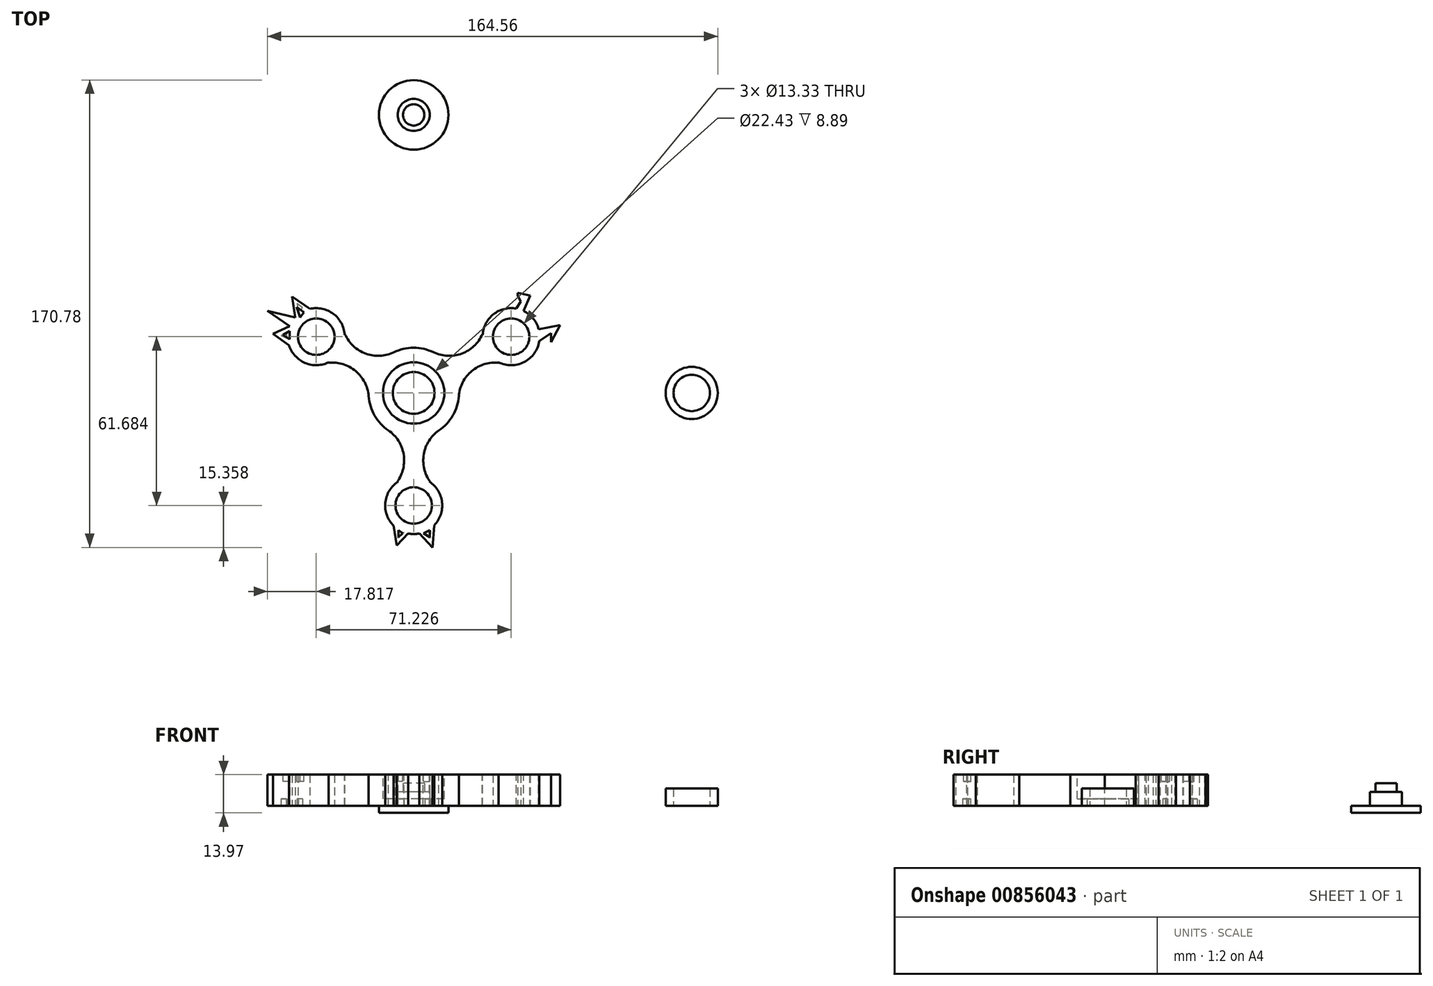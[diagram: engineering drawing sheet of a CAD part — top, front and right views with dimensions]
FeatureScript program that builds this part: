
annotation { "Feature Type Name" : "Feature", "Feature Type Description" : "" }
export const myFeature = defineFeature(function(context is Context, id is Id, definition is map)
    precondition{}
    {
        {
            var Q0;
            Q0=qCreatedBy(makeId("Top.planeOp"),FACE);
            var sketch = newSketch(context, id + "F0", { "sketchPlane" : qUnion([Q0])});
            skCircle(sketch, "E0", {"center": v(0, 101.6) * mm, "radius": 5.85 * mm});
            skSolve(sketch);
        }
        {
            var Q0;
            Q0=qSketchRegion(id+"F0",true);
            extrude(context, id + "F1", {"entities" : qUnion([Q0]), "depth" : 5.08 * mm, "offsetDistance" : 25.4 * mm});
        }
        {
            var Q0;
            Q0=makeQuery(id+"F1.opExtrude","CAP_FACE",FACE,{"disambiguationData":[OSD([sQuery(id+"F0.wireOp",EDGE,"E0")])],"isStart":false});
            var sketch = newSketch(context, id + "F2", { "sketchPlane" : qUnion([Q0])});
            skCircle(sketch, "E1", {"center": v(0, 101.6) * mm, "radius": 3.9 * mm});
            skSolve(sketch);
        }
        {
            var Q0;
            Q0=qSketchRegion(id+"F2",true);
            extrude(context, id + "F3", {"entities" : qUnion([Q0]), "operationType" : NewBodyOperationType.ADD, "depth" : 3.17 * mm, "offsetDistance" : 25.4 * mm});
        }
        {
            var Q0;
            Q0=makeQuery(id+"F1.opExtrude","CAP_FACE",FACE,{"disambiguationData":[OSD([sQuery(id+"F0.wireOp",EDGE,"E0")])],"isStart":true});
            var sketch = newSketch(context, id + "F4", { "sketchPlane" : qUnion([Q0])});
            skCircle(sketch, "E2", {"center": v(0, -101.6) * mm, "radius": 12.7 * mm});
            skSolve(sketch);
        }
        {
            var Q0;
            Q0=qSketchRegion(id+"F4",true);
            extrude(context, id + "F5", {"entities" : qUnion([Q0]), "operationType" : NewBodyOperationType.ADD, "depth" : 2.54 * mm, "offsetDistance" : 25.4 * mm});
        }
        {
            var Q0;
            Q0=qCreatedBy(makeId("Top.planeOp"),FACE);
            var sketch = newSketch(context, id + "F6", { "sketchPlane" : qUnion([Q0])});
            skCircle(sketch, "E3", {"center": v(101.6, 0) * mm, "radius": 9.53 * mm});
            skCircle(sketch, "E4", {"center": v(101.6, 0) * mm, "radius": 6.67 * mm});
            skSolve(sketch);
        }
        {
            var Q0;
            Q0=qSketchRegion(id+"F6",true);
            extrude(context, id + "F7", {"entities" : qUnion([Q0]), "depth" : 6.35 * mm, "offsetDistance" : 25.4 * mm});
        }
        {
            var Q0;
            Q0=qCreatedBy(makeId("Top.planeOp"),FACE);
            var sketch = newSketch(context, id + "F8", { "sketchPlane" : qUnion([Q0])});
            skCircle(sketch, "E5", {"center": v(0, 0) * mm, "radius": 16.51 * mm});
            skCircle(sketch, "E6", {"center": v(0, 0) * mm, "radius": 7.62 * mm});
            skSolve(sketch);
        }
        {
            var Q0;
            Q0=qSketchRegion(id+"F8",true);
            extrude(context, id + "F9", {"entities" : qUnion([Q0]), "depth" : 11.43 * mm, "offsetDistance" : 25.4 * mm});
        }
        {
            var Q0;
            Q0=makeQuery(id+"F9.opExtrude","CAP_FACE",FACE,{"disambiguationData":[OSD([sQuery(id+"F8.wireOp",EDGE,"E5"),sQuery(id+"F8.wireOp",EDGE,"E6")])],"isStart":false});
            var sketch = newSketch(context, id + "F10", { "sketchPlane" : qUnion([Q0])});
            skCircle(sketch, "E7", {"center": v(0, 0) * mm, "radius": 11.21 * mm});
            skSolve(sketch);
        }
        {
            var Q0;
            Q0=qSketchRegion(id+"F10",true);
            extrude(context, id + "F11", {"entities" : qUnion([Q0]), "operationType" : NewBodyOperationType.REMOVE, "oppositeDirection" : true, "depth" : 8.9 * mm, "offsetDistance" : 25.4 * mm});
        }
        {
            var Q0;
            Q0=makeQuery(id+"F9.opExtrude","CAP_FACE",FACE,{"disambiguationData":[OSD([sQuery(id+"F8.wireOp",EDGE,"E5"),sQuery(id+"F8.wireOp",EDGE,"E6")])],"isStart":false});
            var sketch = newSketch(context, id + "F12", { "sketchPlane" : qUnion([Q0])});
            skLineSegment(sketch, "E8", {"start": v(0, -38.1) * mm, "end": v(0, 0) * mm, "construction": true});
            skLineSegment(sketch, "E9", {"start": v(9.21, -13.7) * mm, "end": v(-9.21, -13.7) * mm});
            skPoint(sketch, "E10.center", {"position": v(0, 0) * mm});
            skLineSegment(sketch, "E11.1.0", {"start": v(7.26, 14.83) * mm, "end": v(16.47, -1.13) * mm});
            skLineSegment(sketch, "E11.2.0", {"start": v(-16.47, -1.13) * mm, "end": v(-7.26, 14.83) * mm});
            skArc(sketch, "E12", {"start": v(9.21, -13.7) * mm, "mid": v(3.68, -22.38) * mm, "end": v(5.99, -32.41) * mm});
            skArc(sketch, "E13.MirrorCS", {"start": v(-9.21, -13.7) * mm, "mid": v(-3.68, -22.38) * mm, "end": v(-5.99, -32.41) * mm});
            skArc(sketch, "E14.1.0", {"start": v(7.26, 14.83) * mm, "mid": v(17.54, 14.38) * mm, "end": v(25.08, 21.4) * mm});
            skArc(sketch, "E14.1.1", {"start": v(16.47, -1.13) * mm, "mid": v(21.22, 8) * mm, "end": v(31.06, 11.02) * mm});
            skArc(sketch, "E14.2.0", {"start": v(-16.47, -1.13) * mm, "mid": v(-21.22, 8) * mm, "end": v(-31.06, 11.02) * mm});
            skArc(sketch, "E14.2.1", {"start": v(-7.26, 14.83) * mm, "mid": v(-17.54, 14.38) * mm, "end": v(-25.08, 21.4) * mm});
            skLineSegment(sketch, "E15", {"start": v(-5.99, -32.41) * mm, "end": v(5.99, -32.41) * mm});
            skLineSegment(sketch, "E16", {"start": v(25.08, 21.4) * mm, "end": v(31.06, 11.02) * mm});
            skLineSegment(sketch, "E17", {"start": v(-31.06, 11.02) * mm, "end": v(-25.08, 21.4) * mm});
            skSolve(sketch);
        }
        {
            var Q0;
            Q0=qSketchRegion(id+"F12",true);
            extrude(context, id + "F13", {"entities" : qUnion([Q0]), "operationType" : NewBodyOperationType.ADD, "oppositeDirection" : true, "depth" : 11.43 * mm, "offsetDistance" : 25.4 * mm});
        }
        {
            var Q0;
            Q0=makeQuery(id+"F13.boolean.opBoolean","MERGE",FACE,{"derivedFrom":[makeQuery(id+"F9.opExtrude","CAP_FACE",FACE,{"disambiguationData":[OSD([sQuery(id+"F8.wireOp",EDGE,"E5"),sQuery(id+"F8.wireOp",EDGE,"E6")])],"isStart":false}),makeQuery(id+"F13.opExtrude","CAP_FACE",FACE,{"disambiguationData":[OSD([sQuery(id+"F12.wireOp",EDGE,"E9"),sQuery(id+"F12.wireOp",EDGE,"E12"),sQuery(id+"F12.wireOp",EDGE,"E13.MirrorCS"),sQuery(id+"F12.wireOp",EDGE,"E15")])],"isStart":true}),makeQuery(id+"F13.opExtrude","CAP_FACE",FACE,{"disambiguationData":[OSD([sQuery(id+"F12.wireOp",EDGE,"E11.1.0"),sQuery(id+"F12.wireOp",EDGE,"E14.1.0"),sQuery(id+"F12.wireOp",EDGE,"E14.1.1"),sQuery(id+"F12.wireOp",EDGE,"E16")])],"isStart":true}),makeQuery(id+"F13.opExtrude","CAP_FACE",FACE,{"disambiguationData":[OSD([sQuery(id+"F12.wireOp",EDGE,"E11.2.0"),sQuery(id+"F12.wireOp",EDGE,"E14.2.0"),sQuery(id+"F12.wireOp",EDGE,"E14.2.1"),sQuery(id+"F12.wireOp",EDGE,"E17")])],"isStart":true})]});
            var sketch = newSketch(context, id + "F14", { "sketchPlane" : qUnion([Q0])});
            skCircle(sketch, "E18", {"center": v(0, -41.12) * mm, "radius": 10.42 * mm});
            skCircle(sketch, "E19.1.0", {"center": v(35.61, 20.56) * mm, "radius": 10.42 * mm});
            skCircle(sketch, "E19.2.0", {"center": v(-35.61, 20.56) * mm, "radius": 10.42 * mm});
            skPoint(sketch, "E19.center", {"position": v(0, 0) * mm});
            skSolve(sketch);
        }
        {
            var Q0;
            Q0 = qSketchRegion(id + "F14", true);
            extrude(context, id + "F15", {"entities" : qUnion([Q0]), "operationType" : NewBodyOperationType.ADD, "oppositeDirection" : true, "depth" : 11.43 * mm, "offsetDistance" : 25.4 * mm});
        }
        {
            var Q0;
            Q0=makeQuery(id+"F15.boolean.opBoolean","MERGE",FACE,{"derivedFrom":[makeQuery(id+"F13.boolean.opBoolean","MERGE",FACE,{"derivedFrom":[makeQuery(id+"F9.opExtrude","CAP_FACE",FACE,{"disambiguationData":[OSD([sQuery(id+"F8.wireOp",EDGE,"E5"),sQuery(id+"F8.wireOp",EDGE,"E6")])],"isStart":true}),makeQuery(id+"F13.opExtrude","CAP_FACE",FACE,{"disambiguationData":[OSD([sQuery(id+"F12.wireOp",EDGE,"E9"),sQuery(id+"F12.wireOp",EDGE,"E12"),sQuery(id+"F12.wireOp",EDGE,"E13.MirrorCS"),sQuery(id+"F12.wireOp",EDGE,"E15")])],"isStart":false}),makeQuery(id+"F13.opExtrude","CAP_FACE",FACE,{"disambiguationData":[OSD([sQuery(id+"F12.wireOp",EDGE,"E11.1.0"),sQuery(id+"F12.wireOp",EDGE,"E14.1.0"),sQuery(id+"F12.wireOp",EDGE,"E14.1.1"),sQuery(id+"F12.wireOp",EDGE,"E16")])],"isStart":false}),makeQuery(id+"F13.opExtrude","CAP_FACE",FACE,{"disambiguationData":[OSD([sQuery(id+"F12.wireOp",EDGE,"E11.2.0"),sQuery(id+"F12.wireOp",EDGE,"E14.2.0"),sQuery(id+"F12.wireOp",EDGE,"E14.2.1"),sQuery(id+"F12.wireOp",EDGE,"E17")])],"isStart":false})]}),makeQuery(id+"F15.opExtrude","CAP_FACE",FACE,{"disambiguationData":[OSD([sQuery(id+"F14.wireOp",EDGE,"E18")])],"isStart":false}),makeQuery(id+"F15.opExtrude","CAP_FACE",FACE,{"disambiguationData":[OSD([sQuery(id+"F14.wireOp",EDGE,"E19.1.0")])],"isStart":false}),makeQuery(id+"F15.opExtrude","CAP_FACE",FACE,{"disambiguationData":[OSD([sQuery(id+"F14.wireOp",EDGE,"E19.2.0")])],"isStart":false})]});
            var sketch = newSketch(context, id + "F16", { "sketchPlane" : qUnion([Q0])});
            skLineSegment(sketch, "E20", {"start": v(-7.32, 48.54) * mm, "end": v(-6.21, 55.73) * mm});
            skLineSegment(sketch, "E21", {"start": v(-6.21, 55.73) * mm, "end": v(-2.06, 51.34) * mm});
            skLineSegment(sketch, "E22", {"start": v(-2.06, 51.34) * mm, "end": v(2.06, 51.34) * mm});
            skLineSegment(sketch, "E23", {"start": v(2.06, 51.34) * mm, "end": v(6.87, 56.48) * mm});
            skLineSegment(sketch, "E24", {"start": v(6.87, 56.48) * mm, "end": v(7.52, 48.34) * mm});
            skLineSegment(sketch, "E25", {"start": v(7.52, 48.34) * mm, "end": v(-7.32, 48.54) * mm});
            skSolve(sketch);
        }
        {
            var Q0;
            Q0 = qSketchRegion(id + "F16", true);
            extrude(context, id + "F17", {"entities" : qUnion([Q0]), "operationType" : NewBodyOperationType.ADD, "oppositeDirection" : true, "depth" : 11.43 * mm, "offsetDistance" : 25.4 * mm});
        }
        {
            var Q0;
            Q0=makeQuery(id+"F17.boolean.opBoolean","MERGE",FACE,{"derivedFrom":[makeQuery(id+"F15.boolean.opBoolean","MERGE",FACE,{"derivedFrom":[makeQuery(id+"F13.boolean.opBoolean","MERGE",FACE,{"derivedFrom":[makeQuery(id+"F9.opExtrude","CAP_FACE",FACE,{"disambiguationData":[OSD([sQuery(id+"F8.wireOp",EDGE,"E5"),sQuery(id+"F8.wireOp",EDGE,"E6")])],"isStart":true}),makeQuery(id+"F13.opExtrude","CAP_FACE",FACE,{"disambiguationData":[OSD([sQuery(id+"F12.wireOp",EDGE,"E9"),sQuery(id+"F12.wireOp",EDGE,"E12"),sQuery(id+"F12.wireOp",EDGE,"E13.MirrorCS"),sQuery(id+"F12.wireOp",EDGE,"E15")])],"isStart":false}),makeQuery(id+"F13.opExtrude","CAP_FACE",FACE,{"disambiguationData":[OSD([sQuery(id+"F12.wireOp",EDGE,"E11.1.0"),sQuery(id+"F12.wireOp",EDGE,"E14.1.0"),sQuery(id+"F12.wireOp",EDGE,"E14.1.1"),sQuery(id+"F12.wireOp",EDGE,"E16")])],"isStart":false}),makeQuery(id+"F13.opExtrude","CAP_FACE",FACE,{"disambiguationData":[OSD([sQuery(id+"F12.wireOp",EDGE,"E11.2.0"),sQuery(id+"F12.wireOp",EDGE,"E14.2.0"),sQuery(id+"F12.wireOp",EDGE,"E14.2.1"),sQuery(id+"F12.wireOp",EDGE,"E17")])],"isStart":false})]}),makeQuery(id+"F15.opExtrude","CAP_FACE",FACE,{"disambiguationData":[OSD([sQuery(id+"F14.wireOp",EDGE,"E18")])],"isStart":false}),makeQuery(id+"F15.opExtrude","CAP_FACE",FACE,{"disambiguationData":[OSD([sQuery(id+"F14.wireOp",EDGE,"E19.1.0")])],"isStart":false}),makeQuery(id+"F15.opExtrude","CAP_FACE",FACE,{"disambiguationData":[OSD([sQuery(id+"F14.wireOp",EDGE,"E19.2.0")])],"isStart":false})]}),makeQuery(id+"F17.opExtrude","CAP_FACE",FACE,{"disambiguationData":[OSD([sQuery(id+"F16.wireOp",EDGE,"E20"),sQuery(id+"F16.wireOp",EDGE,"E21"),sQuery(id+"F16.wireOp",EDGE,"E22"),sQuery(id+"F16.wireOp",EDGE,"E23"),sQuery(id+"F16.wireOp",EDGE,"E24"),sQuery(id+"F16.wireOp",EDGE,"E25")])],"isStart":true})]});
            var sketch = newSketch(context, id + "F18", { "sketchPlane" : qUnion([Q0])});
            skLineSegment(sketch, "E26", {"start": v(-37.94, -30.72) * mm, "end": v(-44.47, -35.25) * mm});
            skLineSegment(sketch, "E27", {"start": v(-44.47, -35.25) * mm, "end": v(-43.33, -27.57) * mm});
            skLineSegment(sketch, "E28", {"start": v(-43.33, -27.57) * mm, "end": v(-53.43, -30) * mm});
            skLineSegment(sketch, "E29", {"start": v(-53.43, -30) * mm, "end": v(-45.31, -24.38) * mm});
            skLineSegment(sketch, "E30", {"start": v(-45.31, -24.38) * mm, "end": v(-51.37, -21.6) * mm});
            skLineSegment(sketch, "E31", {"start": v(-51.37, -21.6) * mm, "end": v(-45.56, -17.46) * mm});
            skLineSegment(sketch, "E32", {"start": v(-37.94, -30.72) * mm, "end": v(-45.56, -17.46) * mm});
            skSolve(sketch);
        }
        {
            var Q0;
            Q0 = qSketchRegion(id + "F18", true);
            extrude(context, id + "F19", {"entities" : qUnion([Q0]), "operationType" : NewBodyOperationType.ADD, "oppositeDirection" : true, "depth" : 11.43 * mm, "offsetDistance" : 25.4 * mm});
        }
        {
            var Q0;
            Q0=makeQuery(id+"F19.boolean.opBoolean","MERGE",FACE,{"derivedFrom":[makeQuery(id+"F17.boolean.opBoolean","MERGE",FACE,{"derivedFrom":[makeQuery(id+"F15.boolean.opBoolean","MERGE",FACE,{"derivedFrom":[makeQuery(id+"F13.boolean.opBoolean","MERGE",FACE,{"derivedFrom":[makeQuery(id+"F9.opExtrude","CAP_FACE",FACE,{"disambiguationData":[OSD([sQuery(id+"F8.wireOp",EDGE,"E5"),sQuery(id+"F8.wireOp",EDGE,"E6")])],"isStart":true}),makeQuery(id+"F13.opExtrude","CAP_FACE",FACE,{"disambiguationData":[OSD([sQuery(id+"F12.wireOp",EDGE,"E9"),sQuery(id+"F12.wireOp",EDGE,"E12"),sQuery(id+"F12.wireOp",EDGE,"E13.MirrorCS"),sQuery(id+"F12.wireOp",EDGE,"E15")])],"isStart":false}),makeQuery(id+"F13.opExtrude","CAP_FACE",FACE,{"disambiguationData":[OSD([sQuery(id+"F12.wireOp",EDGE,"E11.1.0"),sQuery(id+"F12.wireOp",EDGE,"E14.1.0"),sQuery(id+"F12.wireOp",EDGE,"E14.1.1"),sQuery(id+"F12.wireOp",EDGE,"E16")])],"isStart":false}),makeQuery(id+"F13.opExtrude","CAP_FACE",FACE,{"disambiguationData":[OSD([sQuery(id+"F12.wireOp",EDGE,"E11.2.0"),sQuery(id+"F12.wireOp",EDGE,"E14.2.0"),sQuery(id+"F12.wireOp",EDGE,"E14.2.1"),sQuery(id+"F12.wireOp",EDGE,"E17")])],"isStart":false})]}),makeQuery(id+"F15.opExtrude","CAP_FACE",FACE,{"disambiguationData":[OSD([sQuery(id+"F14.wireOp",EDGE,"E18")])],"isStart":false}),makeQuery(id+"F15.opExtrude","CAP_FACE",FACE,{"disambiguationData":[OSD([sQuery(id+"F14.wireOp",EDGE,"E19.1.0")])],"isStart":false}),makeQuery(id+"F15.opExtrude","CAP_FACE",FACE,{"disambiguationData":[OSD([sQuery(id+"F14.wireOp",EDGE,"E19.2.0")])],"isStart":false})]}),makeQuery(id+"F17.opExtrude","CAP_FACE",FACE,{"disambiguationData":[OSD([sQuery(id+"F16.wireOp",EDGE,"E20"),sQuery(id+"F16.wireOp",EDGE,"E21"),sQuery(id+"F16.wireOp",EDGE,"E22"),sQuery(id+"F16.wireOp",EDGE,"E23"),sQuery(id+"F16.wireOp",EDGE,"E24"),sQuery(id+"F16.wireOp",EDGE,"E25")])],"isStart":true})]}),makeQuery(id+"F19.opExtrude","CAP_FACE",FACE,{"disambiguationData":[OSD([sQuery(id+"F18.wireOp",EDGE,"E26"),sQuery(id+"F18.wireOp",EDGE,"E27"),sQuery(id+"F18.wireOp",EDGE,"E28"),sQuery(id+"F18.wireOp",EDGE,"E29"),sQuery(id+"F18.wireOp",EDGE,"E30"),sQuery(id+"F18.wireOp",EDGE,"E31"),sQuery(id+"F18.wireOp",EDGE,"E32")])],"isStart":true})]});
            var sketch = newSketch(context, id + "F20", { "sketchPlane" : qUnion([Q0])});
            skLineSegment(sketch, "E33", {"start": v(-40.65, -31.07) * mm, "end": v(-42.7, -32.62) * mm});
            skLineSegment(sketch, "E34", {"start": v(-42.7, -32.62) * mm, "end": v(-42.2, -29.76) * mm});
            skLineSegment(sketch, "E35", {"start": v(-40.65, -31.07) * mm, "end": v(-42.2, -29.76) * mm});
            skLineSegment(sketch, "E36", {"start": v(-46.58, -21.77) * mm, "end": v(-48.45, -20.91) * mm});
            skLineSegment(sketch, "E37", {"start": v(-48.45, -20.91) * mm, "end": v(-46.18, -19.98) * mm});
            skLineSegment(sketch, "E38", {"start": v(-46.58, -21.77) * mm, "end": v(-46.18, -19.98) * mm});
            skSolve(sketch);
        }
        {
            var Q0;
            Q0 = qSketchRegion(id + "F20", true);
            extrude(context, id + "F21", {"entities" : qUnion([Q0]), "operationType" : NewBodyOperationType.REMOVE, "oppositeDirection" : true, "depth" : 2.54 * mm, "offsetDistance" : 25.4 * mm});
        }
        {
            var Q0;
            Q0=makeQuery(id+"F19.boolean.opBoolean","MERGE",FACE,{"derivedFrom":[makeQuery(id+"F17.boolean.opBoolean","MERGE",FACE,{"derivedFrom":[makeQuery(id+"F15.boolean.opBoolean","MERGE",FACE,{"derivedFrom":[makeQuery(id+"F13.boolean.opBoolean","MERGE",FACE,{"derivedFrom":[makeQuery(id+"F9.opExtrude","CAP_FACE",FACE,{"disambiguationData":[OSD([sQuery(id+"F8.wireOp",EDGE,"E5"),sQuery(id+"F8.wireOp",EDGE,"E6")])],"isStart":true}),makeQuery(id+"F13.opExtrude","CAP_FACE",FACE,{"disambiguationData":[OSD([sQuery(id+"F12.wireOp",EDGE,"E9"),sQuery(id+"F12.wireOp",EDGE,"E12"),sQuery(id+"F12.wireOp",EDGE,"E13.MirrorCS"),sQuery(id+"F12.wireOp",EDGE,"E15")])],"isStart":false}),makeQuery(id+"F13.opExtrude","CAP_FACE",FACE,{"disambiguationData":[OSD([sQuery(id+"F12.wireOp",EDGE,"E11.1.0"),sQuery(id+"F12.wireOp",EDGE,"E14.1.0"),sQuery(id+"F12.wireOp",EDGE,"E14.1.1"),sQuery(id+"F12.wireOp",EDGE,"E16")])],"isStart":false}),makeQuery(id+"F13.opExtrude","CAP_FACE",FACE,{"disambiguationData":[OSD([sQuery(id+"F12.wireOp",EDGE,"E11.2.0"),sQuery(id+"F12.wireOp",EDGE,"E14.2.0"),sQuery(id+"F12.wireOp",EDGE,"E14.2.1"),sQuery(id+"F12.wireOp",EDGE,"E17")])],"isStart":false})]}),makeQuery(id+"F15.opExtrude","CAP_FACE",FACE,{"disambiguationData":[OSD([sQuery(id+"F14.wireOp",EDGE,"E18")])],"isStart":false}),makeQuery(id+"F15.opExtrude","CAP_FACE",FACE,{"disambiguationData":[OSD([sQuery(id+"F14.wireOp",EDGE,"E19.1.0")])],"isStart":false}),makeQuery(id+"F15.opExtrude","CAP_FACE",FACE,{"disambiguationData":[OSD([sQuery(id+"F14.wireOp",EDGE,"E19.2.0")])],"isStart":false})]}),makeQuery(id+"F17.opExtrude","CAP_FACE",FACE,{"disambiguationData":[OSD([sQuery(id+"F16.wireOp",EDGE,"E20"),sQuery(id+"F16.wireOp",EDGE,"E21"),sQuery(id+"F16.wireOp",EDGE,"E22"),sQuery(id+"F16.wireOp",EDGE,"E23"),sQuery(id+"F16.wireOp",EDGE,"E24"),sQuery(id+"F16.wireOp",EDGE,"E25")])],"isStart":true})]}),makeQuery(id+"F19.opExtrude","CAP_FACE",FACE,{"disambiguationData":[OSD([sQuery(id+"F18.wireOp",EDGE,"E26"),sQuery(id+"F18.wireOp",EDGE,"E27"),sQuery(id+"F18.wireOp",EDGE,"E28"),sQuery(id+"F18.wireOp",EDGE,"E29"),sQuery(id+"F18.wireOp",EDGE,"E30"),sQuery(id+"F18.wireOp",EDGE,"E31"),sQuery(id+"F18.wireOp",EDGE,"E32")])],"isStart":true})]});
            var sketch = newSketch(context, id + "F22", { "sketchPlane" : qUnion([Q0])});
            skLineSegment(sketch, "E39", {"start": v(45.91, -18.95) * mm, "end": v(50.22, -21.8) * mm});
            skLineSegment(sketch, "E40", {"start": v(50.22, -21.8) * mm, "end": v(50.22, -18.53) * mm});
            skLineSegment(sketch, "E41", {"start": v(50.22, -18.53) * mm, "end": v(53.47, -24.82) * mm});
            skLineSegment(sketch, "E42", {"start": v(53.47, -24.82) * mm, "end": v(43.8, -22.88) * mm});
            skLineSegment(sketch, "E43", {"start": v(43.8, -22.88) * mm, "end": v(39.08, -27.66) * mm});
            skLineSegment(sketch, "E44", {"start": v(39.08, -27.66) * mm, "end": v(42.59, -35.63) * mm});
            skLineSegment(sketch, "E45", {"start": v(42.59, -35.63) * mm, "end": v(38.04, -36.55) * mm});
            skLineSegment(sketch, "E46", {"start": v(38.04, -35.63) * mm, "end": v(38.04, -36.55) * mm});
            skLineSegment(sketch, "E47", {"start": v(38.04, -35.63) * mm, "end": v(39.08, -33.36) * mm});
            skLineSegment(sketch, "E48", {"start": v(39.08, -33.36) * mm, "end": v(35.48, -27.66) * mm});
            skLineSegment(sketch, "E49", {"start": v(45.91, -18.95) * mm, "end": v(43.8, -18.52) * mm});
            skLineSegment(sketch, "E50", {"start": v(43.8, -18.52) * mm, "end": v(35.48, -26.65) * mm});
            skLineSegment(sketch, "E51", {"start": v(35.48, -26.65) * mm, "end": v(35.48, -27.66) * mm});
            skSolve(sketch);
        }
        {
            var Q0;
            Q0 = qSketchRegion(id + "F22", true);
            extrude(context, id + "F23", {"entities" : qUnion([Q0]), "operationType" : NewBodyOperationType.ADD, "oppositeDirection" : true, "depth" : 11.43 * mm, "offsetDistance" : 25.4 * mm});
        }
        {
            var Q0;
            Q0=makeQuery(id+"F23.boolean.opBoolean","MERGE",FACE,{"derivedFrom":[makeQuery(id+"F19.boolean.opBoolean","MERGE",FACE,{"derivedFrom":[makeQuery(id+"F17.boolean.opBoolean","MERGE",FACE,{"derivedFrom":[makeQuery(id+"F15.boolean.opBoolean","MERGE",FACE,{"derivedFrom":[makeQuery(id+"F13.boolean.opBoolean","MERGE",FACE,{"derivedFrom":[makeQuery(id+"F9.opExtrude","CAP_FACE",FACE,{"disambiguationData":[OSD([sQuery(id+"F8.wireOp",EDGE,"E5"),sQuery(id+"F8.wireOp",EDGE,"E6")])],"isStart":true}),makeQuery(id+"F13.opExtrude","CAP_FACE",FACE,{"disambiguationData":[OSD([sQuery(id+"F12.wireOp",EDGE,"E9"),sQuery(id+"F12.wireOp",EDGE,"E12"),sQuery(id+"F12.wireOp",EDGE,"E13.MirrorCS"),sQuery(id+"F12.wireOp",EDGE,"E15")])],"isStart":false}),makeQuery(id+"F13.opExtrude","CAP_FACE",FACE,{"disambiguationData":[OSD([sQuery(id+"F12.wireOp",EDGE,"E11.1.0"),sQuery(id+"F12.wireOp",EDGE,"E14.1.0"),sQuery(id+"F12.wireOp",EDGE,"E14.1.1"),sQuery(id+"F12.wireOp",EDGE,"E16")])],"isStart":false}),makeQuery(id+"F13.opExtrude","CAP_FACE",FACE,{"disambiguationData":[OSD([sQuery(id+"F12.wireOp",EDGE,"E11.2.0"),sQuery(id+"F12.wireOp",EDGE,"E14.2.0"),sQuery(id+"F12.wireOp",EDGE,"E14.2.1"),sQuery(id+"F12.wireOp",EDGE,"E17")])],"isStart":false})]}),makeQuery(id+"F15.opExtrude","CAP_FACE",FACE,{"disambiguationData":[OSD([sQuery(id+"F14.wireOp",EDGE,"E18")])],"isStart":false}),makeQuery(id+"F15.opExtrude","CAP_FACE",FACE,{"disambiguationData":[OSD([sQuery(id+"F14.wireOp",EDGE,"E19.1.0")])],"isStart":false}),makeQuery(id+"F15.opExtrude","CAP_FACE",FACE,{"disambiguationData":[OSD([sQuery(id+"F14.wireOp",EDGE,"E19.2.0")])],"isStart":false})]}),makeQuery(id+"F17.opExtrude","CAP_FACE",FACE,{"disambiguationData":[OSD([sQuery(id+"F16.wireOp",EDGE,"E20"),sQuery(id+"F16.wireOp",EDGE,"E21"),sQuery(id+"F16.wireOp",EDGE,"E22"),sQuery(id+"F16.wireOp",EDGE,"E23"),sQuery(id+"F16.wireOp",EDGE,"E24"),sQuery(id+"F16.wireOp",EDGE,"E25")])],"isStart":true})]}),makeQuery(id+"F19.opExtrude","CAP_FACE",FACE,{"disambiguationData":[OSD([sQuery(id+"F18.wireOp",EDGE,"E26"),sQuery(id+"F18.wireOp",EDGE,"E27"),sQuery(id+"F18.wireOp",EDGE,"E28"),sQuery(id+"F18.wireOp",EDGE,"E29"),sQuery(id+"F18.wireOp",EDGE,"E30"),sQuery(id+"F18.wireOp",EDGE,"E31"),sQuery(id+"F18.wireOp",EDGE,"E32")])],"isStart":true})]}),makeQuery(id+"F23.opExtrude","CAP_FACE",FACE,{"disambiguationData":[OSD([sQuery(id+"F22.wireOp",EDGE,"E39"),sQuery(id+"F22.wireOp",EDGE,"E40"),sQuery(id+"F22.wireOp",EDGE,"E41"),sQuery(id+"F22.wireOp",EDGE,"E42"),sQuery(id+"F22.wireOp",EDGE,"E43"),sQuery(id+"F22.wireOp",EDGE,"E44"),sQuery(id+"F22.wireOp",EDGE,"E45"),sQuery(id+"F22.wireOp",EDGE,"E46"),sQuery(id+"F22.wireOp",EDGE,"E47"),sQuery(id+"F22.wireOp",EDGE,"E48"),sQuery(id+"F22.wireOp",EDGE,"E49"),sQuery(id+"F22.wireOp",EDGE,"E50"),sQuery(id+"F22.wireOp",EDGE,"E51")])],"isStart":true})]});
            var sketch = newSketch(context, id + "F24", { "sketchPlane" : qUnion([Q0])});
            skLineSegment(sketch, "E52", {"start": v(-5.81, 50.25) * mm, "end": v(-5.81, 53.07) * mm});
            skLineSegment(sketch, "E53", {"start": v(-5.81, 53.07) * mm, "end": v(-3.55, 51.03) * mm});
            skLineSegment(sketch, "E54", {"start": v(-5.81, 50.25) * mm, "end": v(-3.55, 51.03) * mm});
            skLineSegment(sketch, "E55", {"start": v(5.97, 53.07) * mm, "end": v(4.13, 51.34) * mm});
            skLineSegment(sketch, "E56", {"start": v(4.13, 51.34) * mm, "end": v(6.1, 50.25) * mm});
            skLineSegment(sketch, "E57", {"start": v(6.1, 50.25) * mm, "end": v(5.97, 53.07) * mm});
            skSolve(sketch);
        }
        {
            var Q0;
            Q0 = qSketchRegion(id + "F24", true);
            extrude(context, id + "F25", {"entities" : qUnion([Q0]), "operationType" : NewBodyOperationType.REMOVE, "oppositeDirection" : true, "depth" : 2.54 * mm, "offsetDistance" : 25.4 * mm});
        }
        {
            var Q0;
            Q0=makeQuery(id+"F23.boolean.opBoolean","MERGE",FACE,{"derivedFrom":[makeQuery(id+"F19.boolean.opBoolean","MERGE",FACE,{"derivedFrom":[makeQuery(id+"F17.boolean.opBoolean","MERGE",FACE,{"derivedFrom":[makeQuery(id+"F15.boolean.opBoolean","MERGE",FACE,{"derivedFrom":[makeQuery(id+"F13.boolean.opBoolean","MERGE",FACE,{"derivedFrom":[makeQuery(id+"F9.opExtrude","CAP_FACE",FACE,{"disambiguationData":[OSD([sQuery(id+"F8.wireOp",EDGE,"E5"),sQuery(id+"F8.wireOp",EDGE,"E6")])],"isStart":true}),makeQuery(id+"F13.opExtrude","CAP_FACE",FACE,{"disambiguationData":[OSD([sQuery(id+"F12.wireOp",EDGE,"E9"),sQuery(id+"F12.wireOp",EDGE,"E12"),sQuery(id+"F12.wireOp",EDGE,"E13.MirrorCS"),sQuery(id+"F12.wireOp",EDGE,"E15")])],"isStart":false}),makeQuery(id+"F13.opExtrude","CAP_FACE",FACE,{"disambiguationData":[OSD([sQuery(id+"F12.wireOp",EDGE,"E11.1.0"),sQuery(id+"F12.wireOp",EDGE,"E14.1.0"),sQuery(id+"F12.wireOp",EDGE,"E14.1.1"),sQuery(id+"F12.wireOp",EDGE,"E16")])],"isStart":false}),makeQuery(id+"F13.opExtrude","CAP_FACE",FACE,{"disambiguationData":[OSD([sQuery(id+"F12.wireOp",EDGE,"E11.2.0"),sQuery(id+"F12.wireOp",EDGE,"E14.2.0"),sQuery(id+"F12.wireOp",EDGE,"E14.2.1"),sQuery(id+"F12.wireOp",EDGE,"E17")])],"isStart":false})]}),makeQuery(id+"F15.opExtrude","CAP_FACE",FACE,{"disambiguationData":[OSD([sQuery(id+"F14.wireOp",EDGE,"E18")])],"isStart":false}),makeQuery(id+"F15.opExtrude","CAP_FACE",FACE,{"disambiguationData":[OSD([sQuery(id+"F14.wireOp",EDGE,"E19.1.0")])],"isStart":false}),makeQuery(id+"F15.opExtrude","CAP_FACE",FACE,{"disambiguationData":[OSD([sQuery(id+"F14.wireOp",EDGE,"E19.2.0")])],"isStart":false})]}),makeQuery(id+"F17.opExtrude","CAP_FACE",FACE,{"disambiguationData":[OSD([sQuery(id+"F16.wireOp",EDGE,"E20"),sQuery(id+"F16.wireOp",EDGE,"E21"),sQuery(id+"F16.wireOp",EDGE,"E22"),sQuery(id+"F16.wireOp",EDGE,"E23"),sQuery(id+"F16.wireOp",EDGE,"E24"),sQuery(id+"F16.wireOp",EDGE,"E25")])],"isStart":true})]}),makeQuery(id+"F19.opExtrude","CAP_FACE",FACE,{"disambiguationData":[OSD([sQuery(id+"F18.wireOp",EDGE,"E26"),sQuery(id+"F18.wireOp",EDGE,"E27"),sQuery(id+"F18.wireOp",EDGE,"E28"),sQuery(id+"F18.wireOp",EDGE,"E29"),sQuery(id+"F18.wireOp",EDGE,"E30"),sQuery(id+"F18.wireOp",EDGE,"E31"),sQuery(id+"F18.wireOp",EDGE,"E32")])],"isStart":true})]}),makeQuery(id+"F23.opExtrude","CAP_FACE",FACE,{"disambiguationData":[OSD([sQuery(id+"F22.wireOp",EDGE,"E39"),sQuery(id+"F22.wireOp",EDGE,"E40"),sQuery(id+"F22.wireOp",EDGE,"E41"),sQuery(id+"F22.wireOp",EDGE,"E42"),sQuery(id+"F22.wireOp",EDGE,"E43"),sQuery(id+"F22.wireOp",EDGE,"E44"),sQuery(id+"F22.wireOp",EDGE,"E45"),sQuery(id+"F22.wireOp",EDGE,"E46"),sQuery(id+"F22.wireOp",EDGE,"E47"),sQuery(id+"F22.wireOp",EDGE,"E48"),sQuery(id+"F22.wireOp",EDGE,"E49"),sQuery(id+"F22.wireOp",EDGE,"E50"),sQuery(id+"F22.wireOp",EDGE,"E51")])],"isStart":true})]});
            var sketch = newSketch(context, id + "F26", { "sketchPlane" : qUnion([Q0])});
            skCircle(sketch, "E58", {"center": v(0, 41.12) * mm, "radius": 6.67 * mm});
            skCircle(sketch, "E59.1.0", {"center": v(-35.61, -20.56) * mm, "radius": 6.67 * mm});
            skCircle(sketch, "E59.2.0", {"center": v(35.61, -20.56) * mm, "radius": 6.67 * mm});
            skPoint(sketch, "E59.center", {"position": v(0, 0) * mm});
            skSolve(sketch);
        }
        {
            var Q0;
            Q0 = qSketchRegion(id + "F26", true);
            extrude(context, id + "F27", {"entities" : qUnion([Q0]), "operationType" : NewBodyOperationType.REMOVE, "oppositeDirection" : true, "depth" : 254 * mm, "offsetDistance" : 25.4 * mm});
        }
        {
            var Q0;
            Q0=makeQuery(id+"F23.boolean.opBoolean","MERGE",FACE,{"derivedFrom":[makeQuery(id+"F19.boolean.opBoolean","MERGE",FACE,{"derivedFrom":[makeQuery(id+"F17.boolean.opBoolean","MERGE",FACE,{"derivedFrom":[makeQuery(id+"F15.boolean.opBoolean","MERGE",FACE,{"derivedFrom":[makeQuery(id+"F13.boolean.opBoolean","MERGE",FACE,{"derivedFrom":[makeQuery(id+"F9.opExtrude","CAP_FACE",FACE,{"disambiguationData":[OSD([sQuery(id+"F8.wireOp",EDGE,"E5"),sQuery(id+"F8.wireOp",EDGE,"E6")])],"isStart":false}),makeQuery(id+"F13.opExtrude","CAP_FACE",FACE,{"disambiguationData":[OSD([sQuery(id+"F12.wireOp",EDGE,"E9"),sQuery(id+"F12.wireOp",EDGE,"E12"),sQuery(id+"F12.wireOp",EDGE,"E13.MirrorCS"),sQuery(id+"F12.wireOp",EDGE,"E15")])],"isStart":true}),makeQuery(id+"F13.opExtrude","CAP_FACE",FACE,{"disambiguationData":[OSD([sQuery(id+"F12.wireOp",EDGE,"E11.1.0"),sQuery(id+"F12.wireOp",EDGE,"E14.1.0"),sQuery(id+"F12.wireOp",EDGE,"E14.1.1"),sQuery(id+"F12.wireOp",EDGE,"E16")])],"isStart":true}),makeQuery(id+"F13.opExtrude","CAP_FACE",FACE,{"disambiguationData":[OSD([sQuery(id+"F12.wireOp",EDGE,"E11.2.0"),sQuery(id+"F12.wireOp",EDGE,"E14.2.0"),sQuery(id+"F12.wireOp",EDGE,"E14.2.1"),sQuery(id+"F12.wireOp",EDGE,"E17")])],"isStart":true})]}),makeQuery(id+"F15.opExtrude","CAP_FACE",FACE,{"disambiguationData":[OSD([sQuery(id+"F14.wireOp",EDGE,"E18")])],"isStart":true}),makeQuery(id+"F15.opExtrude","CAP_FACE",FACE,{"disambiguationData":[OSD([sQuery(id+"F14.wireOp",EDGE,"E19.1.0")])],"isStart":true}),makeQuery(id+"F15.opExtrude","CAP_FACE",FACE,{"disambiguationData":[OSD([sQuery(id+"F14.wireOp",EDGE,"E19.2.0")])],"isStart":true})]}),makeQuery(id+"F17.opExtrude","CAP_FACE",FACE,{"disambiguationData":[OSD([sQuery(id+"F16.wireOp",EDGE,"E20"),sQuery(id+"F16.wireOp",EDGE,"E21"),sQuery(id+"F16.wireOp",EDGE,"E22"),sQuery(id+"F16.wireOp",EDGE,"E23"),sQuery(id+"F16.wireOp",EDGE,"E24"),sQuery(id+"F16.wireOp",EDGE,"E25")])],"isStart":false})]}),makeQuery(id+"F19.opExtrude","CAP_FACE",FACE,{"disambiguationData":[OSD([sQuery(id+"F18.wireOp",EDGE,"E26"),sQuery(id+"F18.wireOp",EDGE,"E27"),sQuery(id+"F18.wireOp",EDGE,"E28"),sQuery(id+"F18.wireOp",EDGE,"E29"),sQuery(id+"F18.wireOp",EDGE,"E30"),sQuery(id+"F18.wireOp",EDGE,"E31"),sQuery(id+"F18.wireOp",EDGE,"E32")])],"isStart":false})]}),makeQuery(id+"F23.opExtrude","CAP_FACE",FACE,{"disambiguationData":[OSD([sQuery(id+"F22.wireOp",EDGE,"E39"),sQuery(id+"F22.wireOp",EDGE,"E40"),sQuery(id+"F22.wireOp",EDGE,"E41"),sQuery(id+"F22.wireOp",EDGE,"E42"),sQuery(id+"F22.wireOp",EDGE,"E43"),sQuery(id+"F22.wireOp",EDGE,"E44"),sQuery(id+"F22.wireOp",EDGE,"E45"),sQuery(id+"F22.wireOp",EDGE,"E46"),sQuery(id+"F22.wireOp",EDGE,"E47"),sQuery(id+"F22.wireOp",EDGE,"E48"),sQuery(id+"F22.wireOp",EDGE,"E49"),sQuery(id+"F22.wireOp",EDGE,"E50"),sQuery(id+"F22.wireOp",EDGE,"E51")])],"isStart":false})]});
            var sketch = newSketch(context, id + "F28", { "sketchPlane" : qUnion([Q0])});
            skLineSegment(sketch, "E60", {"start": v(5.9, -52.73) * mm, "end": v(5.9, -50.14) * mm});
            skLineSegment(sketch, "E61", {"start": v(5.9, -50.14) * mm, "end": v(3.53, -51.33) * mm});
            skLineSegment(sketch, "E62", {"start": v(3.53, -51.33) * mm, "end": v(5.9, -52.73) * mm});
            skLineSegment(sketch, "E63", {"start": v(-4.1, -51.34) * mm, "end": v(-5.57, -52.73) * mm});
            skLineSegment(sketch, "E64", {"start": v(-5.57, -52.73) * mm, "end": v(-5.57, -50.14) * mm});
            skLineSegment(sketch, "E65", {"start": v(-5.57, -50.14) * mm, "end": v(-4.1, -51.34) * mm});
            skSolve(sketch);
        }
        {
            var Q0;
            Q0 = qSketchRegion(id + "F28", true);
            extrude(context, id + "F29", {"entities" : qUnion([Q0]), "operationType" : NewBodyOperationType.REMOVE, "oppositeDirection" : true, "depth" : 2.54 * mm, "offsetDistance" : 25.4 * mm});
        }
        {
            var Q0;
            Q0=makeQuery(id+"F23.boolean.opBoolean","MERGE",FACE,{"derivedFrom":[makeQuery(id+"F19.boolean.opBoolean","MERGE",FACE,{"derivedFrom":[makeQuery(id+"F17.boolean.opBoolean","MERGE",FACE,{"derivedFrom":[makeQuery(id+"F15.boolean.opBoolean","MERGE",FACE,{"derivedFrom":[makeQuery(id+"F13.boolean.opBoolean","MERGE",FACE,{"derivedFrom":[makeQuery(id+"F9.opExtrude","CAP_FACE",FACE,{"disambiguationData":[OSD([sQuery(id+"F8.wireOp",EDGE,"E5"),sQuery(id+"F8.wireOp",EDGE,"E6")])],"isStart":false}),makeQuery(id+"F13.opExtrude","CAP_FACE",FACE,{"disambiguationData":[OSD([sQuery(id+"F12.wireOp",EDGE,"E9"),sQuery(id+"F12.wireOp",EDGE,"E12"),sQuery(id+"F12.wireOp",EDGE,"E13.MirrorCS"),sQuery(id+"F12.wireOp",EDGE,"E15")])],"isStart":true}),makeQuery(id+"F13.opExtrude","CAP_FACE",FACE,{"disambiguationData":[OSD([sQuery(id+"F12.wireOp",EDGE,"E11.1.0"),sQuery(id+"F12.wireOp",EDGE,"E14.1.0"),sQuery(id+"F12.wireOp",EDGE,"E14.1.1"),sQuery(id+"F12.wireOp",EDGE,"E16")])],"isStart":true}),makeQuery(id+"F13.opExtrude","CAP_FACE",FACE,{"disambiguationData":[OSD([sQuery(id+"F12.wireOp",EDGE,"E11.2.0"),sQuery(id+"F12.wireOp",EDGE,"E14.2.0"),sQuery(id+"F12.wireOp",EDGE,"E14.2.1"),sQuery(id+"F12.wireOp",EDGE,"E17")])],"isStart":true})]}),makeQuery(id+"F15.opExtrude","CAP_FACE",FACE,{"disambiguationData":[OSD([sQuery(id+"F14.wireOp",EDGE,"E18")])],"isStart":true}),makeQuery(id+"F15.opExtrude","CAP_FACE",FACE,{"disambiguationData":[OSD([sQuery(id+"F14.wireOp",EDGE,"E19.1.0")])],"isStart":true}),makeQuery(id+"F15.opExtrude","CAP_FACE",FACE,{"disambiguationData":[OSD([sQuery(id+"F14.wireOp",EDGE,"E19.2.0")])],"isStart":true})]}),makeQuery(id+"F17.opExtrude","CAP_FACE",FACE,{"disambiguationData":[OSD([sQuery(id+"F16.wireOp",EDGE,"E20"),sQuery(id+"F16.wireOp",EDGE,"E21"),sQuery(id+"F16.wireOp",EDGE,"E22"),sQuery(id+"F16.wireOp",EDGE,"E23"),sQuery(id+"F16.wireOp",EDGE,"E24"),sQuery(id+"F16.wireOp",EDGE,"E25")])],"isStart":false})]}),makeQuery(id+"F19.opExtrude","CAP_FACE",FACE,{"disambiguationData":[OSD([sQuery(id+"F18.wireOp",EDGE,"E26"),sQuery(id+"F18.wireOp",EDGE,"E27"),sQuery(id+"F18.wireOp",EDGE,"E28"),sQuery(id+"F18.wireOp",EDGE,"E29"),sQuery(id+"F18.wireOp",EDGE,"E30"),sQuery(id+"F18.wireOp",EDGE,"E31"),sQuery(id+"F18.wireOp",EDGE,"E32")])],"isStart":false})]}),makeQuery(id+"F23.opExtrude","CAP_FACE",FACE,{"disambiguationData":[OSD([sQuery(id+"F22.wireOp",EDGE,"E39"),sQuery(id+"F22.wireOp",EDGE,"E40"),sQuery(id+"F22.wireOp",EDGE,"E41"),sQuery(id+"F22.wireOp",EDGE,"E42"),sQuery(id+"F22.wireOp",EDGE,"E43"),sQuery(id+"F22.wireOp",EDGE,"E44"),sQuery(id+"F22.wireOp",EDGE,"E45"),sQuery(id+"F22.wireOp",EDGE,"E46"),sQuery(id+"F22.wireOp",EDGE,"E47"),sQuery(id+"F22.wireOp",EDGE,"E48"),sQuery(id+"F22.wireOp",EDGE,"E49"),sQuery(id+"F22.wireOp",EDGE,"E50"),sQuery(id+"F22.wireOp",EDGE,"E51")])],"isStart":false})]});
            var sketch = newSketch(context, id + "F30", { "sketchPlane" : qUnion([Q0])});
            skLineSegment(sketch, "E66", {"start": v(-40.13, 29.51) * mm, "end": v(-42.83, 31.39) * mm});
            skLineSegment(sketch, "E67", {"start": v(-42.83, 31.39) * mm, "end": v(-41.48, 27.57) * mm});
            skPoint(sketch, "E67.endSnap0", {"position": v(-41.48, 30.45) * mm});
            skLineSegment(sketch, "E68", {"start": v(-40.13, 29.51) * mm, "end": v(-41.48, 27.57) * mm});
            skLineSegment(sketch, "E69", {"start": v(-45.31, 21.17) * mm, "end": v(-44.47, 20.59) * mm});
            skLineSegment(sketch, "E70", {"start": v(-45.31, 19.53) * mm, "end": v(-47.67, 21.17) * mm});
            skPoint(sketch, "E70.startSnap0", {"position": v(-48.47, 19.53) * mm});
            skLineSegment(sketch, "E71", {"start": v(-47.67, 21.17) * mm, "end": v(-45.31, 22.57) * mm});
            skLineSegment(sketch, "E72", {"start": v(-45.31, 22.57) * mm, "end": v(-45.31, 19.53) * mm});
            skSolve(sketch);
        }
        {
            var Q0;
            Q0 = qSketchRegion(id + "F30", true);
            extrude(context, id + "F31", {"entities" : qUnion([Q0]), "operationType" : NewBodyOperationType.REMOVE, "oppositeDirection" : true, "depth" : 2.54 * mm, "offsetDistance" : 25.4 * mm});
        }
    });
